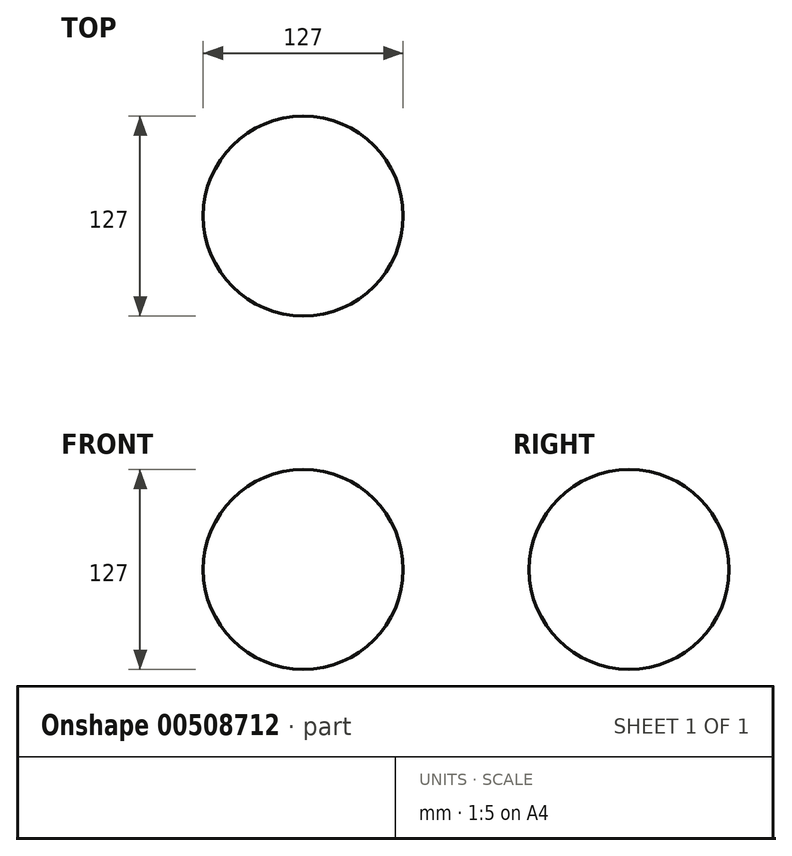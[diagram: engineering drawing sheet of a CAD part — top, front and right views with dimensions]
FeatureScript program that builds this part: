
annotation { "Feature Type Name" : "Feature", "Feature Type Description" : "" }
export const myFeature = defineFeature(function(context is Context, id is Id, definition is map)
    precondition{}
    {
        {
            var Q0;
            Q0=qCreatedBy(makeId("Right.planeOp"),FACE);
            var sketch = newSketch(context, id + "F0", { "sketchPlane" : qUnion([Q0])});
            skArc(sketch, "E0", {"start": v(0, 0) * mm, "mid": v(63.5, 63.5) * mm, "end": v(0, 127) * mm});
            skLineSegment(sketch, "E1", {"start": v(0, 127) * mm, "end": v(0, 0) * mm});
            skSolve(sketch);
        }
        {
            var Q0;
            Q0=makeQuery(id+"F0.imprint","IMPRINT",FACE,{"disambiguationData":[TD([[makeQuery(id+"F0.imprint","IMPRINT",EDGE,{"derivedFrom":sQuery(id+"F0.wireOp",EDGE,"E0")}),1.0]])]});
            var Q1;
            Q1=sQuery(id+"F0.wireOp",EDGE,"E1");
            revolve(context, id + "F1", {"entities" : qUnion([Q0]), "axis" : qUnion([Q1]), "revolveType" : RevolveType.FULL});
        }
    });
